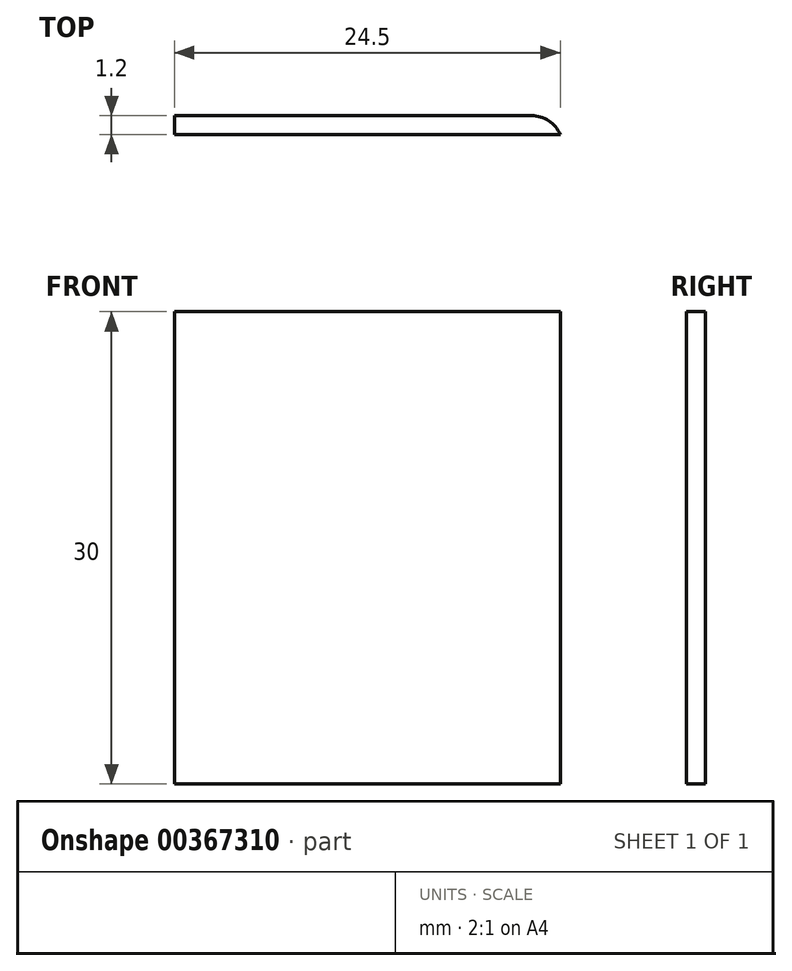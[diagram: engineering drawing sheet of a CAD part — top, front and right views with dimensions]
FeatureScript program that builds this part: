
annotation { "Feature Type Name" : "Feature", "Feature Type Description" : "" }
export const myFeature = defineFeature(function(context is Context, id is Id, definition is map)
    precondition{}
    {
        {
            var Q0;
            Q0=qCreatedBy(makeId("Front.planeOp"),FACE);
            var sketch = newSketch(context, id + "F0", { "sketchPlane" : qUnion([Q0])});
            skLineSegment(sketch, "E0.bottom", {"start": v(-12.25, 15) * mm, "end": v(12.25, 15) * mm});
            skLineSegment(sketch, "E0.top", {"start": v(-12.25, -15) * mm, "end": v(12.25, -15) * mm});
            skLineSegment(sketch, "E0.left", {"start": v(-12.25, 15) * mm, "end": v(-12.25, -15) * mm});
            skLineSegment(sketch, "E0.right", {"start": v(12.25, 15) * mm, "end": v(12.25, -15) * mm});
            skSolve(sketch);
        }
        {
            var Q0;
            Q0 = qSketchRegion(id + "F0", true);
            extrude(context, id + "F1", {"entities" : qUnion([Q0]), "depth" : 1.2 * mm});
        }
        {
            var Q0;
            Q0=makeQuery(id+"F1.opExtrude","CAP_EDGE",EDGE,{"disambiguationData":[OSD([sQuery(id+"F0.wireOp",EDGE,"E0.right")])],"isStart":true});
            fillet(context, id + "F2", {"entities" : qUnion([Q0]), "radius" : 2 * mm, "tangentPropagation" : true, "allowEdgeOverflow" : false});
        }
    });
